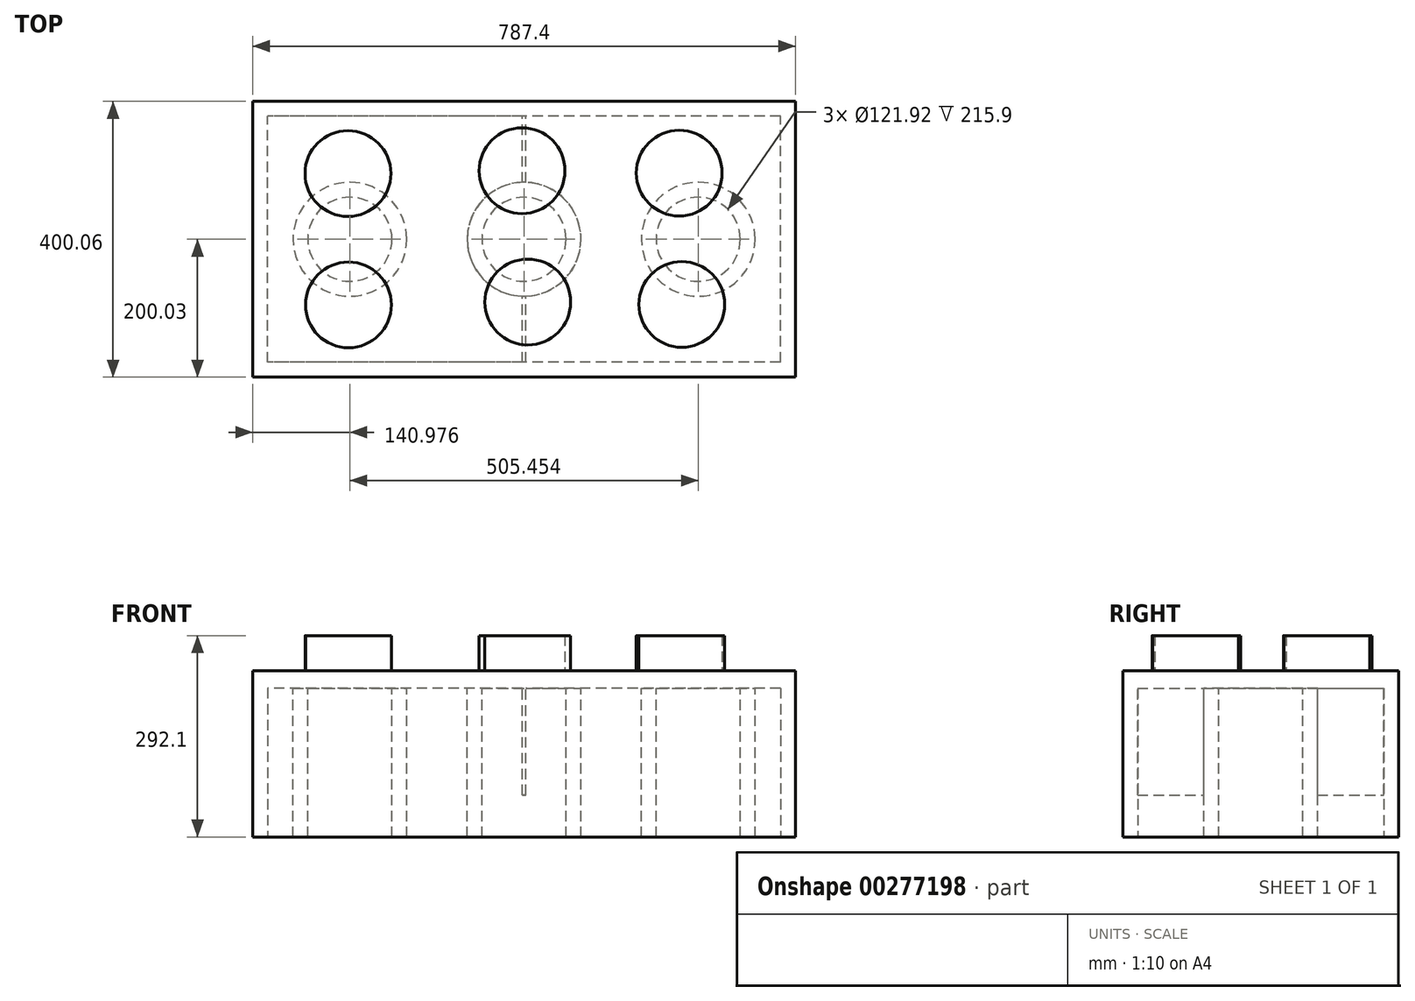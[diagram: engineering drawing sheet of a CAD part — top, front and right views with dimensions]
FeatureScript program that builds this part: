
annotation { "Feature Type Name" : "Feature", "Feature Type Description" : "" }
export const myFeature = defineFeature(function(context is Context, id is Id, definition is map)
    precondition{}
    {
        {
            var Q0;
            Q0=qCreatedBy(makeId("Top.planeOp"),FACE);
            var sketch = newSketch(context, id + "F0", { "sketchPlane" : qUnion([Q0])});
            skLineSegment(sketch, "E0.bottom", {"start": v(393.7, 200.03) * mm, "end": v(-393.7, 200.03) * mm});
            skLineSegment(sketch, "E0.top", {"start": v(393.7, -200.03) * mm, "end": v(-393.7, -200.03) * mm});
            skLineSegment(sketch, "E0.left", {"start": v(393.7, 200.03) * mm, "end": v(393.7, -200.03) * mm});
            skLineSegment(sketch, "E0.right", {"start": v(-393.7, 200.03) * mm, "end": v(-393.7, -200.03) * mm});
            skPoint(sketch, "E0.middle", {"position": v(0, 0) * mm});
            skSolve(sketch);
        }
        {
            var Q0;
            Q0 = qSketchRegion(id + "F0", true);
            extrude(context, id + "F1", {"entities" : qUnion([Q0]), "depth" : 241.3 * mm});
        }
        {
            var Q0;
            Q0=makeQuery(id+"F1.opExtrude","CAP_FACE",FACE,{"disambiguationData":[OSD([sQuery(id+"F0.wireOp",EDGE,"E0.bottom"),sQuery(id+"F0.wireOp",EDGE,"E0.top"),sQuery(id+"F0.wireOp",EDGE,"E0.left"),sQuery(id+"F0.wireOp",EDGE,"E0.right")])],"isStart":false});
            var sketch = newSketch(context, id + "F2", { "sketchPlane" : qUnion([Q0])});
            skCircle(sketch, "E1", {"center": v(-255.57, 95.27) * mm, "radius": 62.23 * mm});
            skCircle(sketch, "E2", {"center": v(-2.94, 99.4) * mm, "radius": 62.23 * mm});
            skCircle(sketch, "E3", {"center": v(225.1, 95.92) * mm, "radius": 62.23 * mm});
            skCircle(sketch, "E4", {"center": v(228.8, -94.58) * mm, "radius": 62.23 * mm});
            skCircle(sketch, "E5", {"center": v(5.4, -91.1) * mm, "radius": 62.23 * mm});
            skCircle(sketch, "E6", {"center": v(-254.74, -95.23) * mm, "radius": 62.23 * mm});
            skSolve(sketch);
        }
        {
            var Q0;
            Q0=makeQuery(id+"F2.imprint","IMPRINT",FACE,{"disambiguationData":[TD([[makeQuery(id+"F2.imprint","IMPRINT",EDGE,{"derivedFrom":sQuery(id+"F2.wireOp",EDGE,"E6")}),1.0]])]});
            var Q1;
            Q1=makeQuery(id+"F2.imprint","IMPRINT",FACE,{"disambiguationData":[TD([[makeQuery(id+"F2.imprint","IMPRINT",EDGE,{"derivedFrom":sQuery(id+"F2.wireOp",EDGE,"E1")}),1.0]])]});
            var Q2;
            Q2=makeQuery(id+"F2.imprint","IMPRINT",FACE,{"disambiguationData":[TD([[makeQuery(id+"F2.imprint","IMPRINT",EDGE,{"derivedFrom":sQuery(id+"F2.wireOp",EDGE,"E2")}),1.0]])]});
            var Q3;
            Q3=makeQuery(id+"F2.imprint","IMPRINT",FACE,{"disambiguationData":[TD([[makeQuery(id+"F2.imprint","IMPRINT",EDGE,{"derivedFrom":sQuery(id+"F2.wireOp",EDGE,"E5")}),1.0]])]});
            var Q4;
            Q4=makeQuery(id+"F2.imprint","IMPRINT",FACE,{"disambiguationData":[TD([[makeQuery(id+"F2.imprint","IMPRINT",EDGE,{"derivedFrom":sQuery(id+"F2.wireOp",EDGE,"E3")}),1.0]])]});
            var Q5;
            Q5=makeQuery(id+"F2.imprint","IMPRINT",FACE,{"disambiguationData":[TD([[makeQuery(id+"F2.imprint","IMPRINT",EDGE,{"derivedFrom":sQuery(id+"F2.wireOp",EDGE,"E4")}),1.0]])]});
            extrude(context, id + "F3", {"entities" : qUnion([Q0, Q1, Q2, Q3, Q4, Q5]), "operationType" : NewBodyOperationType.ADD, "depth" : 50.8 * mm});
        }
        {
            var Q0;
            Q0=makeQuery(id+"F1.opExtrude","CAP_FACE",FACE,{"disambiguationData":[OSD([sQuery(id+"F0.wireOp",EDGE,"E0.bottom"),sQuery(id+"F0.wireOp",EDGE,"E0.top"),sQuery(id+"F0.wireOp",EDGE,"E0.left"),sQuery(id+"F0.wireOp",EDGE,"E0.right")])],"isStart":true});
            var sketch = newSketch(context, id + "F4", { "sketchPlane" : qUnion([Q0])});
            skLineSegment(sketch, "E7.bottom", {"start": v(372.1, 178.44) * mm, "end": v(-372.1, 178.44) * mm});
            skLineSegment(sketch, "E7.top", {"start": v(372.1, -178.43) * mm, "end": v(-372.1, -178.44) * mm});
            skLineSegment(sketch, "E7.left", {"start": v(372.1, 178.44) * mm, "end": v(372.1, -178.44) * mm});
            skLineSegment(sketch, "E7.right", {"start": v(-372.1, 178.44) * mm, "end": v(-372.1, -178.44) * mm});
            skPoint(sketch, "E7.middle", {"position": v(0, 0) * mm});
            skSolve(sketch);
        }
        {
            var Q0;
            Q0=makeQuery(id+"F4.imprint","IMPRINT",FACE,{"disambiguationData":[TD([[makeQuery(id+"F4.imprint","IMPRINT",EDGE,{"derivedFrom":sQuery(id+"F4.wireOp",EDGE,"E7.bottom")}),1.0]])]});
            extrude(context, id + "F5", {"entities" : qUnion([Q0]), "operationType" : NewBodyOperationType.REMOVE, "oppositeDirection" : true, "depth" : 215.9 * mm});
        }
        {
            var Q0;
            Q0=makeQuery(id+"F5.boolean.opBoolean","COPY",FACE,{"derivedFrom":makeQuery(id+"F5.opExtrude","CAP_FACE",FACE,{"disambiguationData":[OSD([sQuery(id+"F4.wireOp",EDGE,"E7.bottom"),sQuery(id+"F4.wireOp",EDGE,"E7.top"),sQuery(id+"F4.wireOp",EDGE,"E7.left"),sQuery(id+"F4.wireOp",EDGE,"E7.right")])],"isStart":false})});
            var sketch = newSketch(context, id + "F6", { "sketchPlane" : qUnion([Q0])});
            skCircle(sketch, "E8", {"center": v(-252.72, 0) * mm, "radius": 82.55 * mm});
            skCircle(sketch, "E9", {"center": v(-252.72, 0) * mm, "radius": 60.96 * mm});
            skCircle(sketch, "E10", {"center": v(0, 0) * mm, "radius": 82.55 * mm});
            skCircle(sketch, "E11", {"center": v(0, 0) * mm, "radius": 60.96 * mm});
            skCircle(sketch, "E12", {"center": v(252.73, 0) * mm, "radius": 82.55 * mm});
            skCircle(sketch, "E13", {"center": v(252.73, 0) * mm, "radius": 60.96 * mm});
            skSolve(sketch);
        }
        {
            var Q0;
            Q0 = qSketchRegion(id + "F6", true);
            extrude(context, id + "F7", {"entities" : qUnion([Q0]), "operationType" : NewBodyOperationType.ADD, "depth" : 215.9 * mm});
        }
        {
            var Q0;
            {var subQ0=sQuery(id+"F4.wireOp",EDGE,"E7.right");var subQ1=sQuery(id+"F4.wireOp",EDGE,"E7.left");var subQ2=sQuery(id+"F4.wireOp",EDGE,"E7.top");var subQ3=sQuery(id+"F4.wireOp",EDGE,"E7.bottom");Q0=makeQuery(id+"F7.boolean.opBoolean","SPLIT",FACE,{"disambiguationData":[TD([makeQuery(id+"F5.boolean.opBoolean","COPY",FACE,{"derivedFrom":makeQuery(id+"F5.opExtrude","SWEPT_FACE",FACE,{"disambiguationData":[OSD([subQ3])]})})])],"derivedFrom":makeQuery(id+"F5.boolean.opBoolean","COPY",FACE,{"derivedFrom":makeQuery(id+"F5.opExtrude","CAP_FACE",FACE,{"disambiguationData":[OSD([subQ3,subQ2,subQ1,subQ0])],"isStart":false})})});}
            var sketch = newSketch(context, id + "F8", { "sketchPlane" : qUnion([Q0])});
            skLineSegment(sketch, "E14.bottom", {"start": v(2.8, 178.44) * mm, "end": v(-2.8, 178.44) * mm});
            skLineSegment(sketch, "E14.top", {"start": v(2.8, -178.44) * mm, "end": v(-2.8, -178.44) * mm});
            skLineSegment(sketch, "E14.left", {"start": v(2.8, 178.44) * mm, "end": v(2.8, -178.44) * mm});
            skLineSegment(sketch, "E14.right", {"start": v(-2.8, 178.44) * mm, "end": v(-2.8, -178.44) * mm});
            skPoint(sketch, "E14.middle", {"position": v(0, 0) * mm});
            skSolve(sketch);
        }
        {
            var Q0;
            Q0 = qSketchRegion(id + "F8", true);
            extrude(context, id + "F9", {"entities" : qUnion([Q0]), "operationType" : NewBodyOperationType.ADD, "depth" : 154.94 * mm});
        }
        {
            var Q0;
            {var subQ0=makeQuery(id+"F7.opExtrude","SWEPT_FACE",FACE,{"disambiguationData":[OSD([sQuery(id+"F6.wireOp",EDGE,"E11")])]});Q0=makeQuery(id+"F9.boolean.opBoolean","SPLIT",FACE,{"disambiguationData":[TD([makeQuery(id+"F9.opExtrude","SWEPT_FACE",FACE,{"disambiguationData":[OSD([sQuery(id+"F8.wireOp",EDGE,"E14.right")])]})])],"derivedFrom":makeQuery(id+"F7.boolean.opBoolean","SPLIT",FACE,{"disambiguationData":[TD([subQ0])],"derivedFrom":makeQuery(id+"F5.boolean.opBoolean","COPY",FACE,{"derivedFrom":makeQuery(id+"F5.opExtrude","CAP_FACE",FACE,{"disambiguationData":[OSD([sQuery(id+"F4.wireOp",EDGE,"E7.bottom"),sQuery(id+"F4.wireOp",EDGE,"E7.top"),sQuery(id+"F4.wireOp",EDGE,"E7.left"),sQuery(id+"F4.wireOp",EDGE,"E7.right")])],"isStart":false})})})});}
            var Q1;
            {var subQ0=makeQuery(id+"F7.opExtrude","SWEPT_FACE",FACE,{"disambiguationData":[OSD([sQuery(id+"F6.wireOp",EDGE,"E11")])]});Q1=makeQuery(id+"F9.boolean.opBoolean","SPLIT",FACE,{"disambiguationData":[TD([makeQuery(id+"F9.opExtrude","SWEPT_FACE",FACE,{"disambiguationData":[OSD([sQuery(id+"F8.wireOp",EDGE,"E14.left")])]})])],"derivedFrom":makeQuery(id+"F7.boolean.opBoolean","SPLIT",FACE,{"disambiguationData":[TD([subQ0])],"derivedFrom":makeQuery(id+"F5.boolean.opBoolean","COPY",FACE,{"derivedFrom":makeQuery(id+"F5.opExtrude","CAP_FACE",FACE,{"disambiguationData":[OSD([sQuery(id+"F4.wireOp",EDGE,"E7.bottom"),sQuery(id+"F4.wireOp",EDGE,"E7.top"),sQuery(id+"F4.wireOp",EDGE,"E7.left"),sQuery(id+"F4.wireOp",EDGE,"E7.right")])],"isStart":false})})})});}
            extrude(context, id + "F10", {"entities" : qUnion([Q0, Q1]), "operationType" : NewBodyOperationType.REMOVE, "depth" : 254 * mm});
        }
        {
            var Q0;
            {var subQ0=sQuery(id+"F8.wireOp",EDGE,"E14.left");var subQ1=sQuery(id+"F8.wireOp",EDGE,"E14.right");Q0=makeQuery(id+"F9.boolean.opBoolean","SPLIT",FACE,{"disambiguationData":[TD([makeQuery(id+"F7.opExtrude","SWEPT_FACE",FACE,{"disambiguationData":[OSD([sQuery(id+"F6.wireOp",EDGE,"E11")])]})])],"derivedFrom":makeQuery(id+"F9.opExtrude","CAP_FACE",FACE,{"disambiguationData":[OSD([sQuery(id+"F8.wireOp",EDGE,"E14.bottom"),sQuery(id+"F8.wireOp",EDGE,"E14.top"),subQ0,subQ1])],"isStart":false})});}
            extrude(context, id + "F11", {"entities" : qUnion([Q0]), "operationType" : NewBodyOperationType.REMOVE, "oppositeDirection" : true, "depth" : 154.94 * mm});
        }
    });
